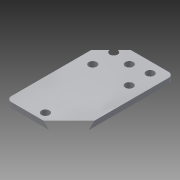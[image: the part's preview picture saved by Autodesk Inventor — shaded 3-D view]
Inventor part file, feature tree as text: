
AUTODESK INVENTOR PART (.ipt)
format: ipt  version: 2014 (Build 180170000, 170)  size: 125,952 bytes
history: native  units: in
note: dims shown in document units (in); Inventor stores cm internally (conversion verified against a paired STEP export)
features: extrude x1, fillet x1, sketch x1
ambient origin geometry x8: Origin, YZ Plane, XZ Plane, XY Plane, X Axis, Y Axis, Z Axis, Center Point
bodies: Solid1 (feature_tree)
feature tree (3):
  extrude  "Extrusion1"  Depth=2.0in
  fillet  "Fillet1"  Radius=0.19in
  sketch  "Sketch1"  dims[d1=0.19in d2=2.0in d3=0.19in d4=0.19in d5=0.5in d6=0.435in d7=0.435in d9=0.19in d10=0.19in d11=0.435in d12=0.5in d15=0.125in d16=0.0in d18=0.3125in d20=1.5in d21=2.5in d22=0.125in d23=0.0625in]
